SOLIDWORKS PART (.sldprt)
format: sldprt  version: not decoded by parser v0  size: 120,320 bytes
history: native  units: mm
features: plane x3, sketch x2, material x1, extrude x1, cut_extrude x1, fillet x1 (+13 scaffold rows collapsed)
feature tree (22):
  scaffold x13  (default folders/planes/origin — collapsed)
  material  "Material <nicht festgelegt>"
  plane  "Ebene vorne"
  plane  "Ebene oben"
  plane  "Ebene rechts"
  sketch  "Skizze1"  dims[D1=75.0mm]
  extrude  "Linear austragen1"  Depth=10mm
  sketch  "Skizze2"  dims[c1.D1=10.0mm c1.D2=100.0mm c1.D3=60.0mm c2.D1=68.0mm c2.D2=52.0mm]
  cut_extrude  "Schnitt-Linear austragen1"  Depth=10mm
  fillet  "Verrundung1"  Radius=3mm
decode coverage: 5 of 5 modeling features carry decoded parameters
note: suppression state not decoded; provenance and decode notes live in map.json
